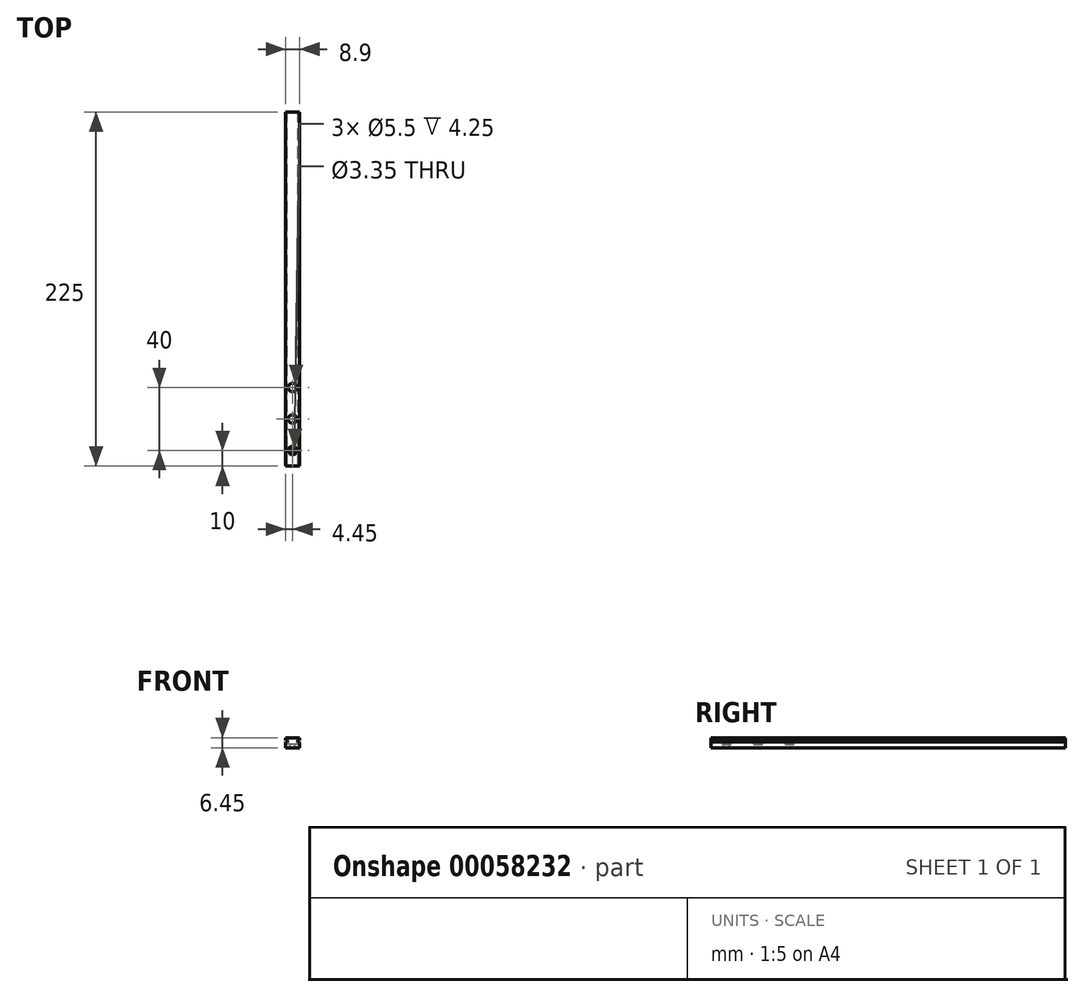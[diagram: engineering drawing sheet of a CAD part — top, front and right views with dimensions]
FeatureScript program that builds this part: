
annotation { "Feature Type Name" : "Feature", "Feature Type Description" : "" }
export const myFeature = defineFeature(function(context is Context, id is Id, definition is map)
    precondition{}
    {
        {
            var Q0;
            Q0=qCreatedBy(makeId("Front.planeOp"),FACE);
            var sketch = newSketch(context, id + "F0", { "sketchPlane" : qUnion([Q0])});
            skLineSegment(sketch, "E0", {"start": v(-4.45, 0) * mm, "end": v(-4.45, 4) * mm});
            skLineSegment(sketch, "E1", {"start": v(-4.45, 4) * mm, "end": v(-3.45, 4) * mm});
            skLineSegment(sketch, "E2", {"start": v(-3.45, 4) * mm, "end": v(-3.45, 4.95) * mm});
            skLineSegment(sketch, "E3", {"start": v(-3.45, 4.95) * mm, "end": v(-4.45, 4.95) * mm});
            skLineSegment(sketch, "E4", {"start": v(-4.45, 4.95) * mm, "end": v(-4.45, 6.45) * mm});
            skLineSegment(sketch, "E5", {"start": v(0, 0) * mm, "end": v(0, 8.72) * mm, "construction": true});
            skLineSegment(sketch, "E6.MirrorCS", {"start": v(4.45, 0) * mm, "end": v(4.45, 4) * mm});
            skLineSegment(sketch, "E7.MirrorCS", {"start": v(4.45, 4) * mm, "end": v(3.45, 4) * mm});
            skLineSegment(sketch, "E8.MirrorCS", {"start": v(3.45, 4.95) * mm, "end": v(4.45, 4.95) * mm});
            skLineSegment(sketch, "E9.MirrorCS", {"start": v(4.45, 4.95) * mm, "end": v(4.45, 6.45) * mm});
            skLineSegment(sketch, "E10.MirrorCS", {"start": v(3.45, 4) * mm, "end": v(3.45, 4.95) * mm});
            skLineSegment(sketch, "E11", {"start": v(-4.45, 0) * mm, "end": v(4.45, 0) * mm});
            skLineSegment(sketch, "E12", {"start": v(-4.45, 6.45) * mm, "end": v(4.45, 6.45) * mm});
            skSolve(sketch);
        }
        {
            var Q0;
            Q0 = qSketchRegion(id + "F0", true);
            extrude(context, id + "F1", {"entities" : qUnion([Q0]), "depth" : 225 * mm});
        }
        {
            var Q0;
            Q0=makeQuery(id+"F1.opExtrude","SWEPT_FACE",FACE,{"disambiguationData":[OSD([sQuery(id+"F0.wireOp",EDGE,"E12")])]});
            var sketch = newSketch(context, id + "F2", { "sketchPlane" : qUnion([Q0])});
            skLineSegment(sketch, "E13", {"start": v(0, -225) * mm, "end": v(0, 0) * mm, "construction": true});
            skCircle(sketch, "E14", {"center": v(0, -215) * mm, "radius": 2.75 * mm});
            skCircle(sketch, "E15.0.1.0", {"center": v(0, -195) * mm, "radius": 2.75 * mm});
            skCircle(sketch, "E15.0.2.0", {"center": v(0, -175) * mm, "radius": 2.75 * mm});
            skLineSegment(sketch, "E15.direction1", {"start": v(0, -215) * mm, "end": v(19.44, -215) * mm, "construction": true});
            skLineSegment(sketch, "E15.direction2", {"start": v(0, -215) * mm, "end": v(0, -195) * mm, "construction": true});
            skSolve(sketch);
        }
        {
            var Q0;
            Q0 = qSketchRegion(id + "F2", true);
            extrude(context, id + "F3", {"entities" : qUnion([Q0]), "operationType" : NewBodyOperationType.REMOVE, "oppositeDirection" : true, "depth" : 4.25 * mm});
        }
        {
            var Q0;
            Q0=makeQuery(id+"F3.boolean.opBoolean","COPY",FACE,{"derivedFrom":makeQuery(id+"F3.opExtrude","CAP_FACE",FACE,{"disambiguationData":[OSD([sQuery(id+"F2.wireOp",EDGE,"E14")])],"isStart":false})});
            var sketch = newSketch(context, id + "F4", { "sketchPlane" : qUnion([Q0])});
            skCircle(sketch, "E16", {"center": v(0, -215) * mm, "radius": 1.68 * mm});
            skSolve(sketch);
        }
        {
            var Q0;
            Q0 = qSketchRegion(id + "F4", true);
            extrude(context, id + "F5", {"entities" : qUnion([Q0]), "operationType" : NewBodyOperationType.REMOVE, "endBound" : BoundingType.THROUGH_ALL, "oppositeDirection" : true, "depth" : 25 * mm});
        }
    });
